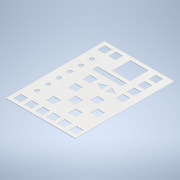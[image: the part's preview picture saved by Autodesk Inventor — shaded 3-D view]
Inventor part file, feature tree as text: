
AUTODESK INVENTOR PART (.ipt)
format: ipt  version: 2021.1 (Build 251245000, 245)  size: 241,152 bytes
history: native  units: mm
features: extrude x3, sketch x3
ambient origin geometry x8: Origin, YZ Plane, XZ Plane, XY Plane, X Axis, Y Axis, Z Axis, Center Point
bodies: Solid1 (feature_tree)
feature tree (6):
  extrude  "Extrusion1"  Depth=1.5875mm TaperAngle=0.0deg
  extrude  "Extrusion2"  [1 undecoded]
  extrude  "Extrusion3"  [1 undecoded]
  sketch  "Sketch1"  dims[d4=1.5875mm d5=0.0mm d6=6.35mm d7=0.0mm]
  sketch  "Sketch2"  dims[d8=6.35mm d9=0.0mm]
  sketch  "Sketch3"
note: 2 required parameter values undecoded (feature->parameter linkage not recoverable at this tier; creation-order binding heuristic only, values carry confidence <= 0.55)
